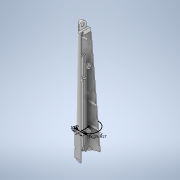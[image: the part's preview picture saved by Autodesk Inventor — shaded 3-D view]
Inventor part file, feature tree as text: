
AUTODESK INVENTOR PART (.ipt)
format: ipt  version: 2021 (Build 250183000, 183)  size: 920,064 bytes
history: native  units: mm
features: sketch x37, extrude x32, plane x16, fillet x5, hole x3, loft x2, revolve x2, other x1, thread x1
ambient origin geometry x8: Origin, YZ Plane, XZ Plane, XY Plane, X Axis, Y Axis, Z Axis, Center Point
bodies: Body1 (feature_tree)
feature tree (99):
  other  "Sólido1"
  plane  "Plano de trabajo1"
  plane  "Plano de trabajo2"
  plane  "Plano de trabajo4"
  plane  "Plano de trabajo5"
  plane  "Plano de trabajo6"
  sketch  "Boceto1"  dims[d1=250.0mm d2=0.0mm d3=-80.0mm d4=-110.0mm]
  sketch  "Boceto2"  dims[d5=-140.0mm d7=-0.0mm d8=2.0mm]
  sketch  "Boceto3"  dims[d9=140.0mm d10=250.0mm]
  sketch  "Boceto4"  dims[d11=24.0mm d22=0.0mm d23=90.0deg d24=0.0mm d25=90.0deg]
  sketch  "Boceto6"  dims[d44=45.0mm d49=29.11157mm]
  sketch  "Boceto7"  dims[d50=29.11157mm d53=29.11157mm]
  loft  "Solevación1"
  fillet  "Empalme2"  [1 undecoded]
  extrude  "Extrusión1"  TaperAngle=0.0deg  [1 undecoded]
  fillet  "Empalme5"  Radius=2.0mm
  plane  "Plano de trabajo7"
  extrude  "Extrusión2"  Depth=250.0mm
  plane  "Plano de trabajo8"
  plane  "Plano de trabajo9"
  loft  "Solevación9"
  plane  "Plano de trabajo10"
  extrude  "Extrusión3"  Depth=29.11157mm
  plane  "Plano de trabajo11"
  revolve  "Revolución1"  [1 undecoded]
  revolve  "Revolución2"  [1 undecoded]
  extrude  "Extrusión4"  Depth=32.5mm
  plane  "Plano de trabajo12"
  extrude  "Extrusión5"  Depth=44.747934mm
  plane  "Plano de trabajo13"
  plane  "Plano de trabajo14"
  extrude  "Extrusión6"  Depth=42.747934mm
  extrude  "Extrusión7"  Depth=42.747934mm
  extrude  "Extrusión8"  Depth=13.0mm
  extrude  "Extrusión11"  Depth=7.75mm
  extrude  "Extrusión9"  Depth=7.75mm
  extrude  "Extrusión10"  Depth=16.0mm
  extrude  "Extrusión12"  Depth=12.0mm
  sketch  "Boceto30"  dims[d160=-19.75mm d161=0.0mm d163=0.0mm d164=2.0mm]
  extrude  "Extrusión13"  Depth=7.75mm
  extrude  "Extrusión14"  Depth=7.75mm
  extrude  "Extrusión15"  TaperAngle=0.0deg  [1 undecoded]
  hole  "Agujero1"  [1 undecoded]
  thread  "Rosca1"  [1 undecoded]
  extrude  "Extrusión16"  Depth=2.0mm
  plane  "Plano de trabajo16"
  extrude  "Extrusión17"  TaperAngle=0.0deg  [1 undecoded]
  extrude  "Extrusión18"  TaperAngle=0.0deg  [1 undecoded]
  fillet  "Empalme6"  [1 undecoded]
  fillet  "Empalme7"  Radius=2.0mm
  plane  "Plano de trabajo17"
  sketch  "Boceto46"  dims[d185=2.0mm d187=1.0mm]
  hole  "Agujero2"  [1 undecoded]
  hole  "Agujero3"  [1 undecoded]
  extrude  "Extrusión21"  [1 undecoded]
  plane  "Plano de trabajo19"
  sketch  "Boceto50"  dims[d193=0.25mm d194=90.0deg]
  extrude  "Extrusión34"  Depth=0.75mm
  extrude  "Extrusión35"  Depth=1.0mm
  extrude  "Extrusión37"  Depth=17.453293mm
  sketch  "Boceto44"  dims[d181=0.75mm d182=0.25mm]
  extrude  "Extrusión23"  Depth=0.75mm
  sketch  "Boceto47"  dims[d189=3.0mm d190=2.0mm]
  extrude  "Extrusión22"  Depth=0.25mm
  sketch  "Boceto45"  dims[d183=1.0mm d184=0.25mm]
  extrude  "Extrusión32"  Depth=0.25mm
  extrude  "Extrusión30"  Depth=2.0mm
  extrude  "Extrusión31"  Depth=2.0mm
  extrude  "Extrusión33"  Depth=2.0mm
  extrude  "Extrusión28"  TaperAngle=90.0deg  [1 undecoded]
  sketch  "Boceto49"  dims[d191=2.0mm d192=0.25mm]
  extrude  "Extrusión24"  [1 undecoded]
  extrude  "Extrusión36"  Depth=2.0mm
  extrude  "Extrusión25"  Depth=2.0mm
  fillet  "Empalme8"  Radius=9.0mm
  sketch  "Boceto9"  dims[d59=29.11157mm d61=29.11157mm]
  sketch  "Boceto10"  dims[d65=22.5mm d66=32.5mm]
  sketch  "Boceto15"  dims[d67=22.5mm d90=44.747934mm]
  sketch  "Boceto16"  dims[d91=42.747934mm d93=42.747934mm]
  sketch  "Boceto17"  dims[d96=0.0mm d97=90.0deg d98=0.0mm d99=90.0deg d100=0.0mm d101=90.0deg d102=0.0mm d103=90.0deg d112=42.747934mm]
  sketch  "Boceto18"  dims[d115=5.0mm d120=13.0mm]
  sketch  "Boceto19"  dims[d121=6.5mm d124=7.75mm]
  sketch  "Boceto20"  dims[d125=7.75mm d126=7.75mm]
  sketch  "Boceto21"  dims[d127=7.75mm d130=16.0mm]
  sketch  "Boceto22"  dims[d131=0.0mm d132=12.0mm]
  sketch  "Boceto24"  dims[d133=12.0mm d134=7.75mm]
  sketch  "Boceto25"  dims[d135=6.5mm d136=7.75mm]
  sketch  "Boceto26"  dims[d137=15.0mm d138=0.0mm]
  sketch  "Boceto27"  dims[d146=-8.5mm d147=30.0mm d148=2.0mm]
  sketch  "Boceto28"  dims[d149=25.12mm d150=2.0mm]
  sketch  "Boceto29"  dims[d151=10.357mm d156=0.0mm d157=90.0deg d158=0.0mm d159=90.0deg]
  sketch  "Boceto31"  dims[d165=15.0mm d166=4.0mm]
  sketch  "Boceto36"  dims[d167=30.0mm d168=12.0mm]
  sketch  "Boceto37"  dims[d169=0.0mm d170=-7.25mm]
  sketch  "Boceto38"  dims[d171=4.5mm d172=0.75mm]
  sketch  "Boceto39"  dims[d173=2.5mm d174=1.0mm]
  sketch  "Boceto40"  dims[d176=11.0mm d177=17.453293mm]
  sketch  "Boceto41"  dims[d179=2.939597mm d180=0.75mm]
  sketch  "Boceto51"  dims[d196=4.381635mm d197=0.0mm d198=-48.25mm d199=12.0mm d200=20.0mm d201=9.0mm d202=9.0mm d203=2.0mm d204=201.75mm d205=0.0mm d206=0.5mm d207=0.25mm d208=-7.5mm d209=100.0mm d210=0.0mm d211=35.0mm d212=0.0mm d213=210.0mm d214=0.0mm d215=2.0mm d216=1.059606mm d217=6.5mm d218=1.059606mm d219=5.0mm d220=2.0mm d221=0.0mm d222=2.0mm d223=6.5mm d224=1.059606mm d225=5.0mm d226=4.5mm d227=2.0mm d228=0.0mm d229=6.0mm d230=10.0mm d231=3.0mm d232=11.0mm d233=10.5mm d235=30.0deg d236=4.75mm d237=0.0mm d238=-17.0mm d239=100.0mm d240=0.0mm d241=6.5mm d242=2.0mm d243=4.0mm d244=15.0mm d245=2.0mm d247=16.0mm d248=2.0mm d249=0.0mm d250=4.5mm d251=0.75mm d252=2.5mm d253=1.0mm d254=11.0mm d255=17.453293mm d256=2.939597mm d257=0.75mm d258=0.75mm d259=0.25mm d260=1.0mm d261=0.25mm d262=2.0mm d263=1.0mm d264=3.0mm d265=2.0mm d266=2.0mm d267=0.25mm d268=0.25mm d269=40.0mm d270=1.0mm d271=1.0mm d272=7.75mm d273=0.5mm d274=8.5mm d275=90.0deg d276=0.0mm d277=17.75mm d280=22.5mm d281=2.0mm d282=0.0mm d283=0.0mm d292=2.0mm d293=0.0mm d296=3.5mm d297=0.0mm d299=4.0mm d300=3.708mm d301=3.023mm d302=2.0mm d303=14.3117mm d304=16.0mm d305=0.0mm d306=16.0mm d307=0.0mm d314=6.0mm d315=19.2mm d316=6.0mm d317=19.2mm d318=13.0mm d320=6.0mm d321=19.2mm d322=13.0mm d323=6.0mm d324=19.2mm d325=13.0mm d326=7.0mm d332=10.0mm d333=0.0mm d335=-41.0mm d336=4.0mm d337=1.0mm d338=9.0mm d339=4.0mm d340=1.0mm d341=9.0mm d342=4.0mm d343=5.2mm d344=4.0mm d345=0.0mm d346=15.0mm d347=5.0mm d349=5.0mm d351=0.0mm d352=45.0mm d354=10.0mm d355=10.0mm d356=0.0mm d357=15.0mm d358=0.0mm d359=2.0mm d363=50.4375mm d376=14.159606mm d377=2.0mm d379=2.0mm d380=11.25mm d381=90.0mm d382=290.0mm d383=14.059606mm d384=100.875mm d390=30.940394mm d391=2.0mm d392=100.875mm d393=14.790546mm d394=2.0mm d395=3.0mm d396=6.0mm d397=4.0mm d398=4.0mm d399=4.0mm d400=8.128453mm d401=12.0mm d402=5.5mm d403=2.5mm d404=2.0mm d405=2.0mm d406=1.0mm d407=2.0mm d408=2.0mm d409=0.0mm d411=50.4375mm d412=6.0mm d418=13.059606mm d419=6.5mm d420=6.5mm d421=50.4375mm d422=126.09375mm d423=0.0mm d424=15.0mm d425=5.0mm d426=5.0mm d427=0.0mm d428=45.0mm d429=10.0mm d430=2.0mm d431=4.0mm d432=6.0mm d433=8.0mm d434=2.0mm d435=90.0deg d436=20.0mm d437=0.0mm d438=4.0mm d439=6.0mm d440=8.0mm d441=2.0mm d442=90.0deg d443=20.0mm d444=0.0mm d446=10.0mm d447=3.0mm d448=11.5mm d450=9.0mm d451=9.0mm d452=90.0mm d453=750.0mm d454=22.5mm d455=43.0mm d456=44.0mm d457=14.159606mm d458=11.25mm d459=2.0mm d460=0.0mm d461=22.5mm d462=43.0mm d463=7.059606mm d464=3.0mm d465=6.0mm d466=3.0mm d467=6.0mm d468=180.0mm d469=0.0mm d470=180.0mm d471=0.0mm d472=4.5mm d473=10.0mm d474=0.0mm d475=7.0mm d476=0.0mm d481=14.059606mm d482=250.0mm d483=2.0mm d484=0.0mm d485=4.0mm d486=4.0mm d487=4.0mm d490=6.0mm d491=0.0mm d492=4.0mm d493=4.0mm d494=0.0mm d495=0.0mm d496=0.0mm d497=0.0mm d498=4.5mm d499=11.0mm d500=0.0mm d501=2.0mm d502=0.0mm d503=61.5mm d504=19.917mm d508=24.0mm d509=56.5mm d510=0.0mm d511=1.5mm d512=2.0mm d513=2.0mm d514=52.5mm d515=0.0mm d516=35.0mm d517=3.0mm d518=150.0deg d520=61.5mm d521=2.0mm d522=2.0mm d523=0.0mm d524=0.5mm d525=25.0mm d526=0.0mm d527=0.5mm d528=0.872665mm d529=0.5mm d530=0.872665mm]
note: 15 required parameter values undecoded (feature->parameter linkage not recoverable at this tier; creation-order binding heuristic only, values carry confidence <= 0.55)